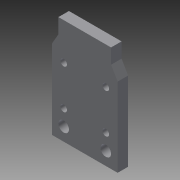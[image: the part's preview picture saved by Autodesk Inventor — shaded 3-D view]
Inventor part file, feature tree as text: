
AUTODESK INVENTOR PART (.ipt)
format: ipt  version: 2013 (Build 170138000, 138)  size: 117,760 bytes
history: native  units: mm
features: sketch x4, extrude x2, hole x2, other x1
ambient origin geometry x8: Origin, YZ Plane, XZ Plane, XY Plane, X Axis, Y Axis, Z Axis, Center Point
feature tree (9):
  other  "ソリッド1"
  extrude  "押し出し1"  Depth=25.0mm
  extrude  "押し出し2"  Depth=40.0mm
  hole  "穴1"  [1 undecoded]
  hole  "穴2"  [1 undecoded]
  sketch  "スケッチ1"
  sketch  "スケッチ2"
  sketch  "スケッチ3"
  sketch  "スケッチ4"
note: 2 required parameter values undecoded (feature->parameter linkage not recoverable at this tier; creation-order binding heuristic only, values carry confidence <= 0.55)
